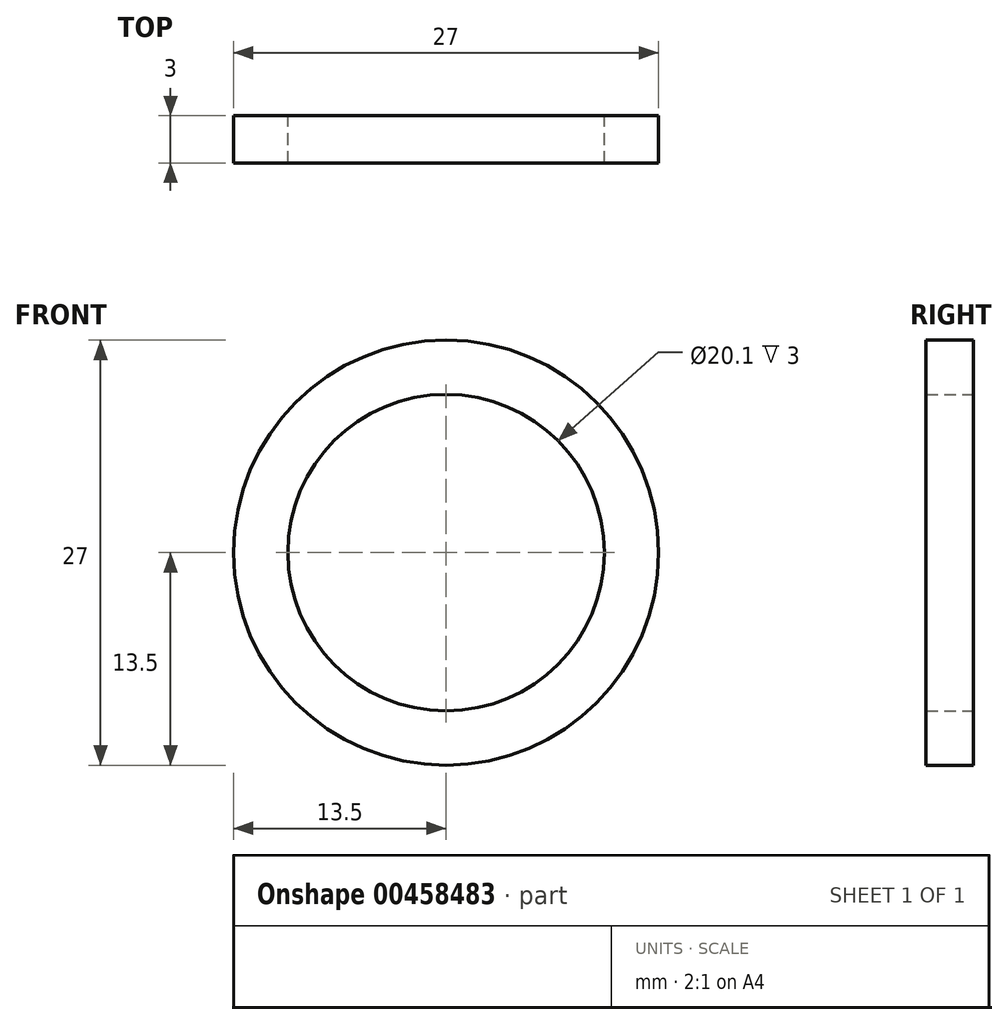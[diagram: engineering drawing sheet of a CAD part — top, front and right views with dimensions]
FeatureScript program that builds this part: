
annotation { "Feature Type Name" : "Feature", "Feature Type Description" : "" }
export const myFeature = defineFeature(function(context is Context, id is Id, definition is map)
    precondition{}
    {
        {
            var Q0;
            Q0=qCreatedBy(makeId("Front.planeOp"),FACE);
            var sketch = newSketch(context, id + "F0", { "sketchPlane" : qUnion([Q0])});
            skCircle(sketch, "E0", {"center": v(0, 0) * mm, "radius": 10.05 * mm});
            skCircle(sketch, "E1", {"center": v(0, 0) * mm, "radius": 13.5 * mm});
            skSolve(sketch);
        }
        {
            var Q0;
            Q0 = qSketchRegion(id + "F0", true);
            extrude(context, id + "F1", {"entities" : qUnion([Q0]), "depth" : 3 * mm});
        }
    });
